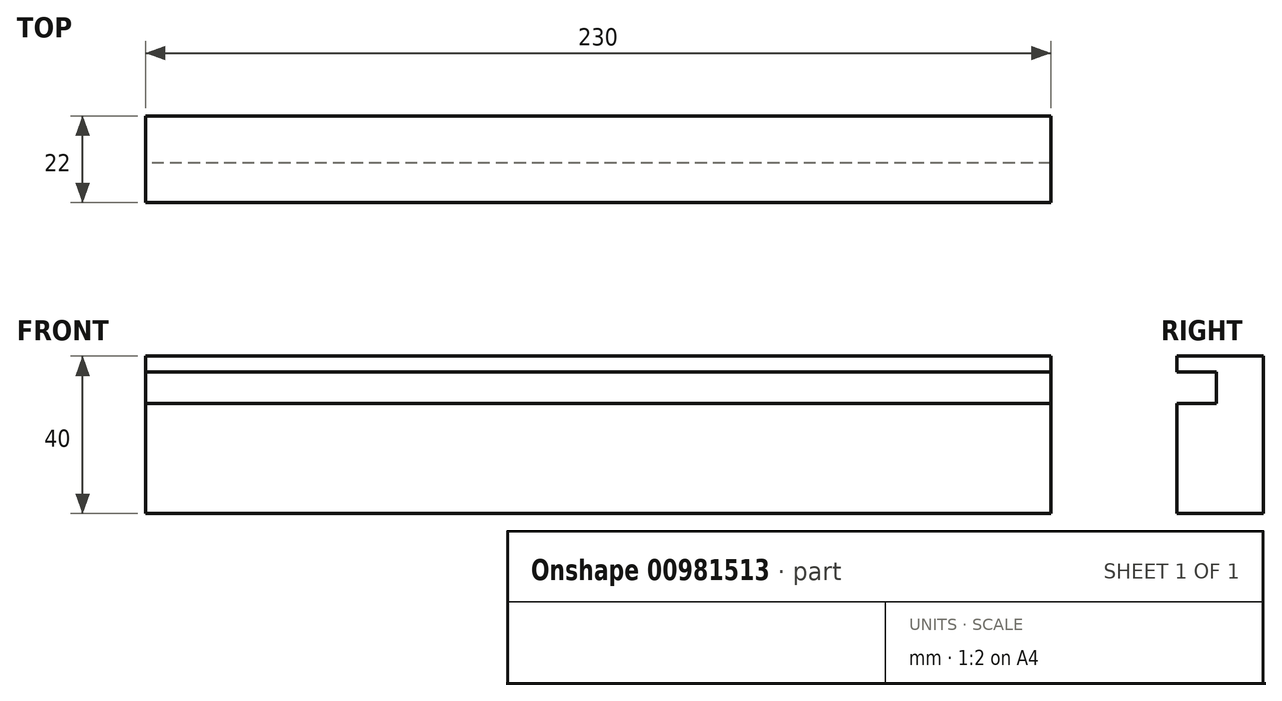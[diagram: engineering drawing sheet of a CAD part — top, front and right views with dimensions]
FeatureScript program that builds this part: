
annotation { "Feature Type Name" : "Feature", "Feature Type Description" : "" }
export const myFeature = defineFeature(function(context is Context, id is Id, definition is map)
    precondition{}
    {
        {
            var Q0;
            Q0=qCreatedBy(makeId("Right.planeOp"),FACE);
            var sketch = newSketch(context, id + "F0", { "sketchPlane" : qUnion([Q0])});
            skLineSegment(sketch, "E0.bottom", {"start": v(-30.65, 67.88) * mm, "end": v(-8.65, 67.88) * mm});
            skLineSegment(sketch, "E0.top", {"start": v(-30.65, 27.88) * mm, "end": v(-8.65, 27.88) * mm});
            skLineSegment(sketch, "E0.left", {"start": v(-30.65, 67.88) * mm, "end": v(-30.65, 27.88) * mm});
            skLineSegment(sketch, "E0.right", {"start": v(-8.65, 67.88) * mm, "end": v(-8.65, 27.88) * mm});
            skLineSegment(sketch, "E1.bottom", {"start": v(-30.65, 63.88) * mm, "end": v(-20.65, 63.88) * mm});
            skLineSegment(sketch, "E1.top", {"start": v(-30.65, 55.88) * mm, "end": v(-20.65, 55.88) * mm});
            skLineSegment(sketch, "E1.left", {"start": v(-30.65, 63.88) * mm, "end": v(-30.65, 55.88) * mm});
            skLineSegment(sketch, "E1.right", {"start": v(-20.65, 63.88) * mm, "end": v(-20.65, 55.88) * mm});
            skSolve(sketch);
        }
        {
            var Q0;
            {var subQ4=sQuery(id+"F0.wireOp",EDGE,"E0.bottom");Q0=makeQuery(id+"F0.imprint","IMPRINT",FACE,{"disambiguationData":[TD([[makeQuery(id+"F0.imprint","IMPRINT",EDGE,{"derivedFrom":subQ4}),-1.0]])]});}
            extrude(context, id + "F1", {"entities" : qUnion([Q0]), "depth" : 230 * mm, "offsetDistance" : 25 * mm});
        }
    });
